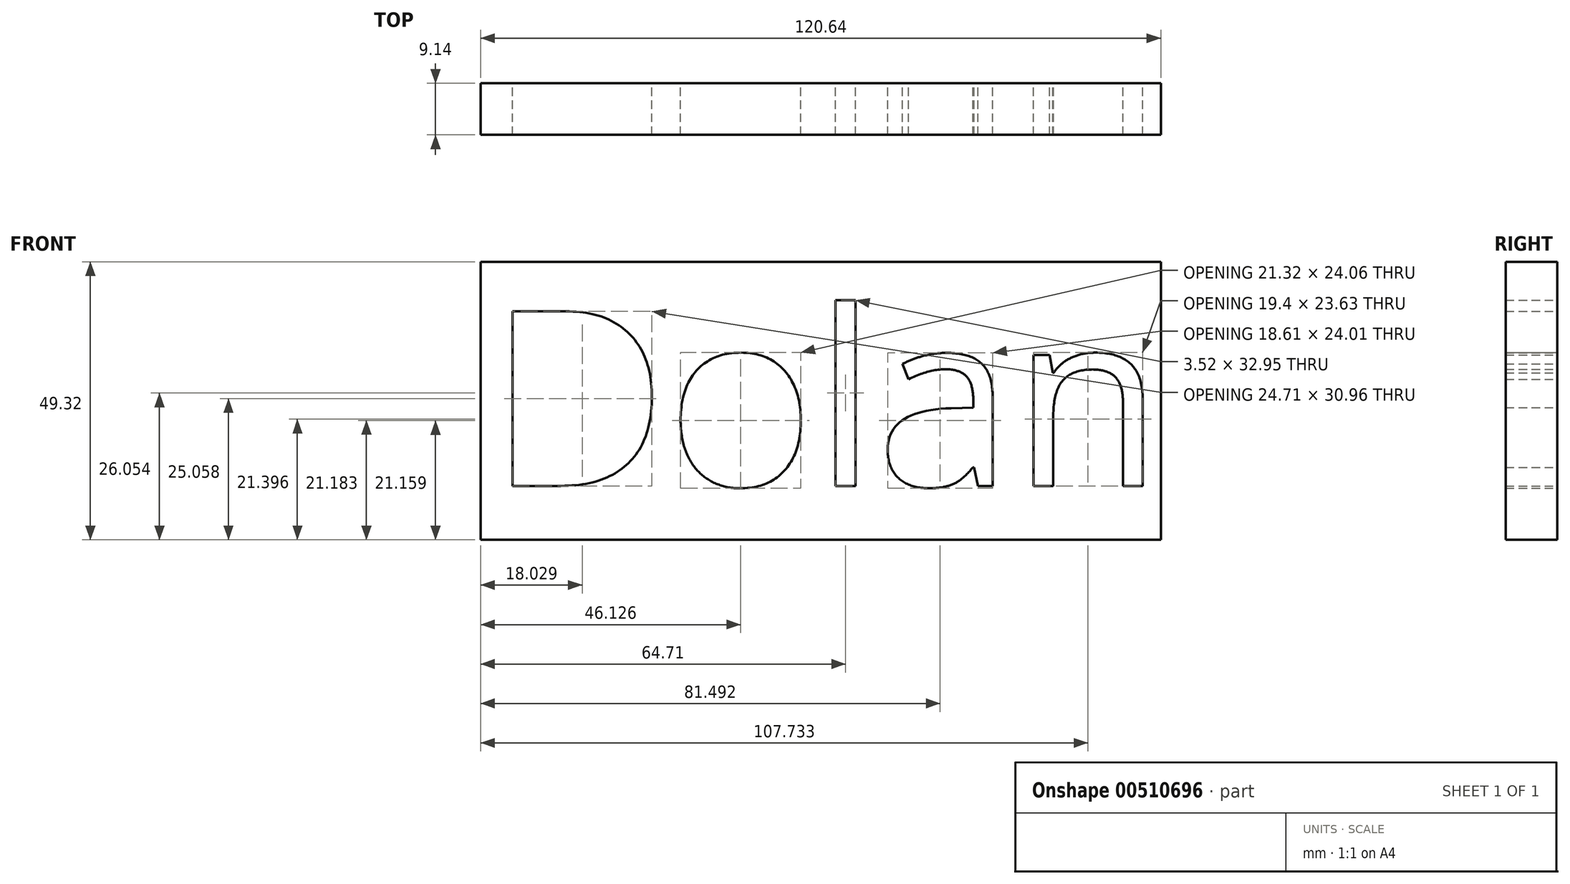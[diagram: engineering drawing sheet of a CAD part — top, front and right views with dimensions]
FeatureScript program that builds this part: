
annotation { "Feature Type Name" : "Feature", "Feature Type Description" : "" }
export const myFeature = defineFeature(function(context is Context, id is Id, definition is map)
    precondition{}
    {
        {
            var Q0;
            Q0=qCreatedBy(makeId("Front.planeOp"),FACE);
            var sketch = newSketch(context, id + "F0", { "sketchPlane" : qUnion([Q0])});
            skText(sketch, "E0", { "text": "Dolan", "fontName": "OpenSans-Regular.ttf"});
            skLineSegment(sketch, "E1.bottom", {"start": v(-57.48, 46.66) * mm, "end": v(63.16, 46.66) * mm});
            skLineSegment(sketch, "E1.top", {"start": v(-57.48, -2.66) * mm, "end": v(63.16, -2.66) * mm});
            skLineSegment(sketch, "E1.left", {"start": v(-57.48, 46.66) * mm, "end": v(-57.48, -2.66) * mm});
            skLineSegment(sketch, "E1.right", {"start": v(63.16, 46.66) * mm, "end": v(63.16, -2.66) * mm});
            const initialGuessF0  = {"E0": [-0.05606, 0.00692, 1, 0, 0.03122]};
            skSetInitialGuess(sketch, initialGuessF0);
            skSolve(sketch);
        }
        {
            var Q0;
            Q0 = qSketchRegion(id + "F0", true);
            extrude(context, id + "F1", {"entities" : qUnion([Q0]), "depth" : 9.14 * mm});
        }
    });
